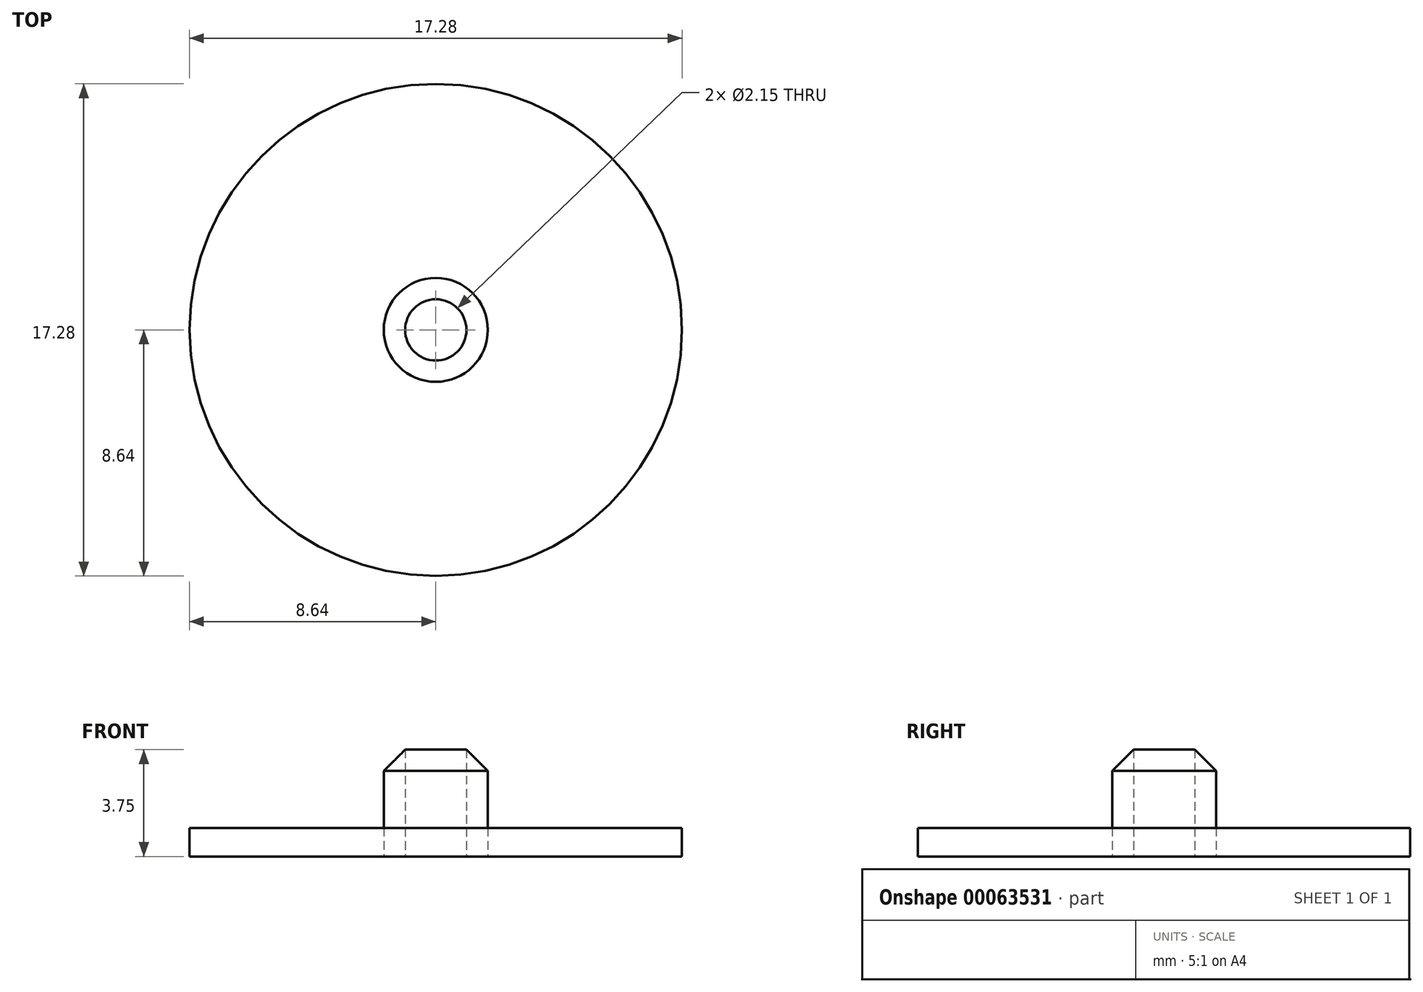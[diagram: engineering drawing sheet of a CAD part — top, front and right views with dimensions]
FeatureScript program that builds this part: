
annotation { "Feature Type Name" : "Feature", "Feature Type Description" : "" }
export const myFeature = defineFeature(function(context is Context, id is Id, definition is map)
    precondition{}
    {
        {
            var Q0;
            Q0=qCreatedBy(makeId("Top.planeOp"),FACE);
            var sketch = newSketch(context, id + "F4", { "sketchPlane" : qUnion([Q0])});
            skCircle(sketch, "E0", {"center": v(0, 0) * mm, "radius": 8.64 * mm});
            skSolve(sketch);
        }
        {
            var Q0;
            Q0 = qSketchRegion(id + "F4", true);
            extrude(context, id + "F0", {"entities" : qUnion([Q0]), "depth" : 1 * mm});
        }
        {
            var Q0;
            Q0=qCreatedBy(makeId("Top.planeOp"),FACE);
            var sketch = newSketch(context, id + "F5", { "sketchPlane" : qUnion([Q0])});
            skCircle(sketch, "E1", {"center": v(0, 0) * mm, "radius": 1.82 * mm});
            skSolve(sketch);
        }
        {
            var Q0;
            Q0 = qSketchRegion(id + "F5", true);
            extrude(context, id + "F1", {"entities" : qUnion([Q0]), "depth" : (1 + 3) * mm});
        }
        {
            var Q0;
            Q0=sQuery(id+"F5.wireOp",VERTEX,"E1.center");
            var Q1;
            Q1=makeQuery(id+"F0.opExtrude","SWEPT_BODY",BODY,{"disambiguationData":[OSD([sQuery(id+"F4.wireOp",EDGE,"E0")])]});
            var Q2;
            Q2=makeQuery(id+"F1.opExtrude","SWEPT_BODY",BODY,{"disambiguationData":[OSD([sQuery(id+"F5.wireOp",EDGE,"E1")])]});
            hole(context, id + "F2", {"style" : HoleStyle.SIMPLE, "holeDiameter" : (1.75 + .4) * mm, "endStyle" : HoleEndStyle.THROUGH, "oppositeDirection" : true, "locations" : qUnion([Q0]), "scope" : qUnion([Q1, Q2])});
        }
        {
            var Q0;
            Q0=makeQuery(id+"F1.opExtrude","CAP_EDGE",EDGE,{"disambiguationData":[OSD([sQuery(id+"F5.wireOp",EDGE,"E1")])],"isStart":false});
            var Q1;
            Q1=makeQuery(id+"F2.hole-0.boolean.opBoolean","COPY",EDGE,{"disambiguationData":[OD(0.0)],"derivedFrom":makeQuery(id+"F2.hole-0.opRevolve","SWEPT_EDGE",EDGE,{"disambiguationData":[OSD([sQuery(id+"F2.hole-0.sketch.wireOp",EDGE,"core_line_2"),sQuery(id+"F2.hole-0.sketch.wireOp",EDGE,"core_line_3")])]})});
            chamfer(context, id + "F3", {"entities" : qUnion([Q0, Q1]), "width" : 1 * mm});
        }
    });
